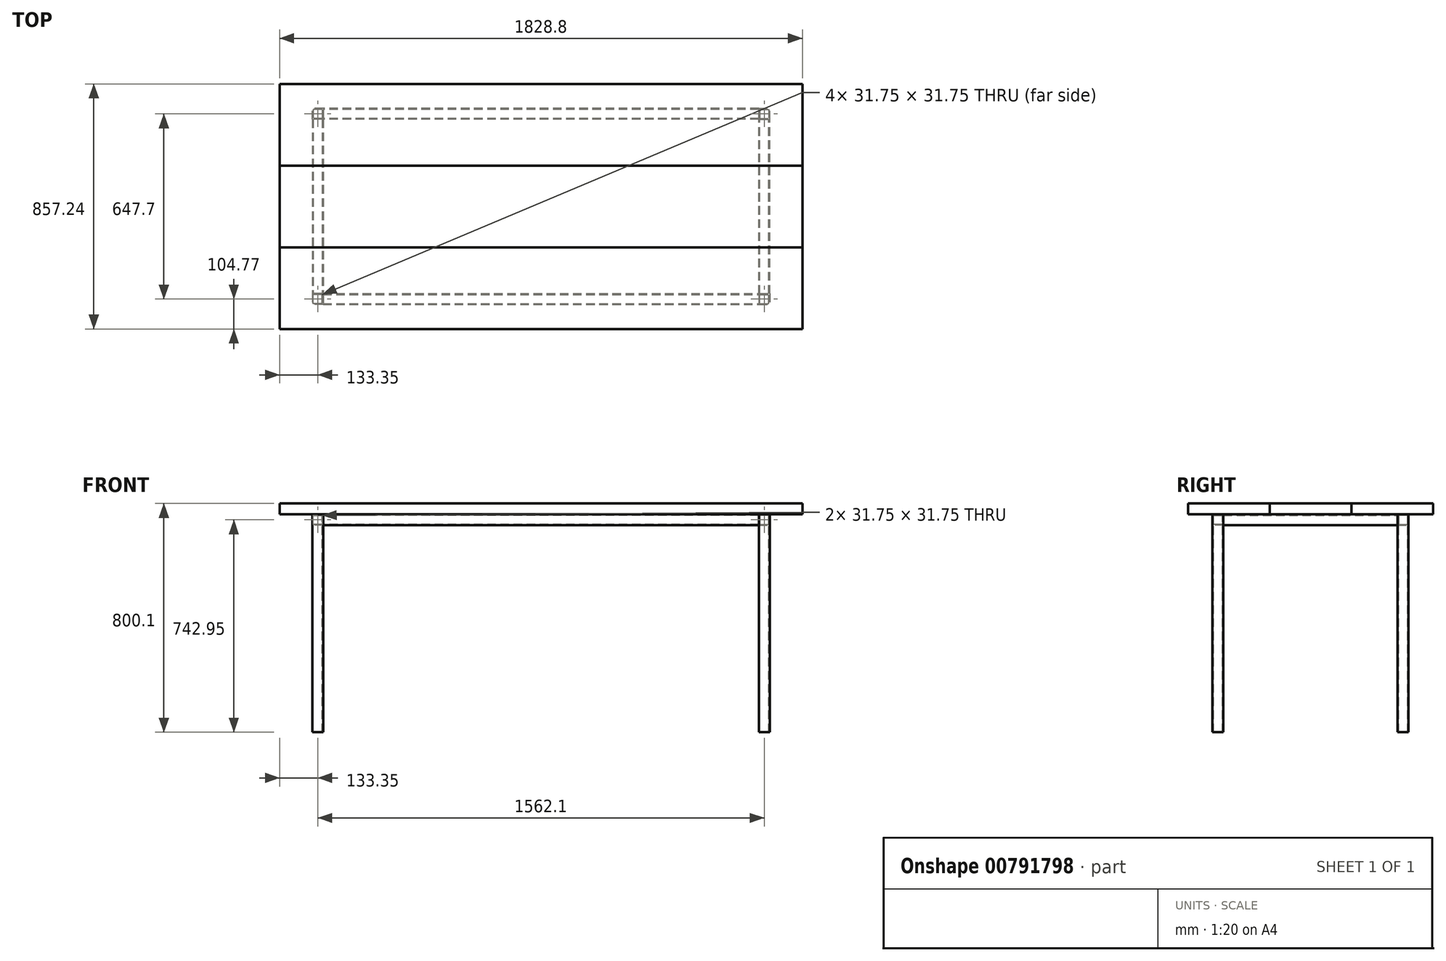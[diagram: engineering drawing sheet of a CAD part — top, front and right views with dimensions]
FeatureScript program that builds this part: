
annotation { "Feature Type Name" : "Feature", "Feature Type Description" : "" }
export const myFeature = defineFeature(function(context is Context, id is Id, definition is map)
    precondition{}
    {
        {
            var Q0;
            Q0=qCreatedBy(makeId("Top.planeOp"),FACE);
            var sketch = newSketch(context, id + "F0", { "sketchPlane" : qUnion([Q0])});
            skLineSegment(sketch, "E0.bottom", {"start": v(781.05, 323.85) * mm, "end": v(-781.05, 323.85) * mm});
            skLineSegment(sketch, "E0.top", {"start": v(781.05, -323.85) * mm, "end": v(-781.05, -323.85) * mm});
            skLineSegment(sketch, "E0.left", {"start": v(781.05, 323.85) * mm, "end": v(781.05, -323.85) * mm});
            skLineSegment(sketch, "E0.right", {"start": v(-781.05, 323.85) * mm, "end": v(-781.05, -323.85) * mm});
            skPoint(sketch, "E0.middle", {"position": v(0, 0) * mm});
            skSolve(sketch);
        }
        {
            var Q0;
            Q0=qCreatedBy(makeId("Front.planeOp"),FACE);
            var sketch = newSketch(context, id + "F1", { "sketchPlane" : qUnion([Q0])});
            skLineSegment(sketch, "E1.0", {"start": v(781.05, 0) * mm, "end": v(-781.05, 0) * mm});
            skLineSegment(sketch, "E2.bottom", {"start": v(-762, 19.05) * mm, "end": v(-800.1, 19.05) * mm});
            skLineSegment(sketch, "E2.top", {"start": v(-762, -19.05) * mm, "end": v(-800.1, -19.05) * mm});
            skLineSegment(sketch, "E2.left", {"start": v(-762, 19.05) * mm, "end": v(-762, -19.05) * mm});
            skLineSegment(sketch, "E2.right", {"start": v(-800.1, 19.05) * mm, "end": v(-800.1, -19.05) * mm});
            skPoint(sketch, "E2.middle", {"position": v(-781.05, 0) * mm});
            skLineSegment(sketch, "E3.bottom", {"start": v(-765.18, 15.87) * mm, "end": v(-796.93, 15.87) * mm});
            skLineSegment(sketch, "E3.top", {"start": v(-765.18, -15.88) * mm, "end": v(-796.93, -15.88) * mm});
            skLineSegment(sketch, "E3.left", {"start": v(-765.18, 15.87) * mm, "end": v(-765.18, -15.87) * mm});
            skLineSegment(sketch, "E3.right", {"start": v(-796.93, 15.87) * mm, "end": v(-796.93, -15.87) * mm});
            skSolve(sketch);
        }
        {
            var Q0;
            {var subQ1=sQuery(id+"F1.wireOp",EDGE,"E2.bottom");Q0=makeQuery(id+"F1.imprint","IMPRINT",FACE,{"disambiguationData":[TD([[makeQuery(id+"F1.imprint","IMPRINT",EDGE,{"derivedFrom":subQ1}),1.0]])]});}
            var Q1;
            Q1=sQuery(id+"F0.wireOp",EDGE,"E0.right");
            var Q2;
            Q2=sQuery(id+"F0.wireOp",EDGE,"E0.top");
            var Q3;
            Q3=sQuery(id+"F0.wireOp",EDGE,"E0.left");
            var Q4;
            Q4=sQuery(id+"F0.wireOp",EDGE,"E0.bottom");
            sweep(context, id + "F2", {"profiles" : qUnion([Q0]), "path" : qUnion([Q1, Q2, Q3, Q4])});
        }
        {
            var Q0;
            Q0=makeQuery(id+"F2.opSweep","SWEPT_FACE",FACE,{"disambiguationData":[OSD([sQuery(id+"F0.wireOp",EDGE,"E0.top"),sQuery(id+"F1.wireOp",EDGE,"E2.bottom")])]});
            var sketch = newSketch(context, id + "F3", { "sketchPlane" : qUnion([Q0])});
            skLineSegment(sketch, "E4.bottom", {"start": v(-762, 304.8) * mm, "end": v(-800.1, 304.8) * mm});
            skLineSegment(sketch, "E4.top", {"start": v(-762, 342.9) * mm, "end": v(-800.1, 342.9) * mm});
            skLineSegment(sketch, "E4.left", {"start": v(-762, 304.8) * mm, "end": v(-762, 342.9) * mm});
            skLineSegment(sketch, "E4.right", {"start": v(-800.1, 304.8) * mm, "end": v(-800.1, 342.9) * mm});
            skLineSegment(sketch, "E5.bottom", {"start": v(762, 304.8) * mm, "end": v(800.1, 304.8) * mm});
            skLineSegment(sketch, "E5.top", {"start": v(762, 342.9) * mm, "end": v(800.1, 342.9) * mm});
            skLineSegment(sketch, "E5.left", {"start": v(762, 304.8) * mm, "end": v(762, 342.9) * mm});
            skLineSegment(sketch, "E5.right", {"start": v(800.1, 304.8) * mm, "end": v(800.1, 342.9) * mm});
            skLineSegment(sketch, "E6.bottom", {"start": v(762, -304.8) * mm, "end": v(800.1, -304.8) * mm});
            skLineSegment(sketch, "E6.top", {"start": v(762, -342.9) * mm, "end": v(800.1, -342.9) * mm});
            skLineSegment(sketch, "E6.left", {"start": v(762, -304.8) * mm, "end": v(762, -342.9) * mm});
            skLineSegment(sketch, "E6.right", {"start": v(800.1, -304.8) * mm, "end": v(800.1, -342.9) * mm});
            skLineSegment(sketch, "E7.bottom", {"start": v(-762, -304.8) * mm, "end": v(-800.1, -304.8) * mm});
            skLineSegment(sketch, "E7.top", {"start": v(-762, -342.9) * mm, "end": v(-800.1, -342.9) * mm});
            skLineSegment(sketch, "E7.left", {"start": v(-762, -304.8) * mm, "end": v(-762, -342.9) * mm});
            skLineSegment(sketch, "E7.right", {"start": v(-800.1, -304.8) * mm, "end": v(-800.1, -342.9) * mm});
            skSolve(sketch);
        }
        {
            var Q0;
            Q0 = qSketchRegion(id + "F3", true);
            extrude(context, id + "F4", {"entities" : qUnion([Q0]), "operationType" : NewBodyOperationType.REMOVE, "oppositeDirection" : true, "depth" : 38.1 * mm, "offsetDistance" : 25.4 * mm});
        }
        {
            var Q0;
            Q0=makeQuery(id+"F4.boolean.opBoolean","SPLIT",FACE,{"disambiguationData":[TD([makeQuery(id+"F4.opExtrude","SWEPT_FACE",FACE,{"disambiguationData":[OSD([sQuery(id+"F3.wireOp",EDGE,"E4.left")])]})])],"derivedFrom":makeQuery(id+"F2.opSweep","SWEPT_FACE",FACE,{"disambiguationData":[OSD([sQuery(id+"F0.wireOp",EDGE,"E0.top"),sQuery(id+"F1.wireOp",EDGE,"E2.bottom")])]})});
            var sketch = newSketch(context, id + "F5", { "sketchPlane" : qUnion([Q0])});
            skLineSegment(sketch, "E8.bottom", {"start": v(-762, 304.8) * mm, "end": v(-800.1, 304.8) * mm});
            skLineSegment(sketch, "E8.top", {"start": v(-762, 342.9) * mm, "end": v(-800.1, 342.9) * mm});
            skLineSegment(sketch, "E8.left", {"start": v(-762, 304.8) * mm, "end": v(-762, 342.9) * mm});
            skLineSegment(sketch, "E8.right", {"start": v(-800.1, 304.8) * mm, "end": v(-800.1, 342.9) * mm});
            skLineSegment(sketch, "E9.bottom", {"start": v(-765.18, 339.73) * mm, "end": v(-796.93, 339.73) * mm});
            skLineSegment(sketch, "E9.top", {"start": v(-765.18, 307.98) * mm, "end": v(-796.93, 307.98) * mm});
            skLineSegment(sketch, "E9.left", {"start": v(-765.18, 339.73) * mm, "end": v(-765.18, 307.97) * mm});
            skLineSegment(sketch, "E9.right", {"start": v(-796.93, 339.73) * mm, "end": v(-796.93, 307.97) * mm});
            skPoint(sketch, "E9.middle", {"position": v(-781.05, 323.85) * mm});
            skPoint(sketch, "E9.middle.positionSnap0", {"position": v(-781.05, 342.9) * mm});
            skPoint(sketch, "E9.middle.positionSnap1", {"position": v(-762, 323.85) * mm});
            skPoint(sketch, "E9.centerSnap0", {"position": v(-781.05, 342.9) * mm});
            skPoint(sketch, "E9.centerSnap1", {"position": v(-762, 323.85) * mm});
            skLineSegment(sketch, "E10.MirrorCS", {"start": v(765.18, 339.73) * mm, "end": v(796.93, 339.73) * mm});
            skLineSegment(sketch, "E11.MirrorCS", {"start": v(762, 342.9) * mm, "end": v(800.1, 342.9) * mm});
            skLineSegment(sketch, "E12.MirrorCS", {"start": v(800.1, 304.8) * mm, "end": v(800.1, 342.9) * mm});
            skLineSegment(sketch, "E13.MirrorCS", {"start": v(796.93, 339.73) * mm, "end": v(796.93, 307.97) * mm});
            skLineSegment(sketch, "E14.MirrorCS", {"start": v(765.18, 307.98) * mm, "end": v(796.93, 307.98) * mm});
            skLineSegment(sketch, "E15.MirrorCS", {"start": v(762, 304.8) * mm, "end": v(800.1, 304.8) * mm});
            skLineSegment(sketch, "E16.MirrorCS", {"start": v(762, 304.8) * mm, "end": v(762, 342.9) * mm});
            skLineSegment(sketch, "E17.MirrorCS", {"start": v(765.18, 339.73) * mm, "end": v(765.18, 307.97) * mm});
            skLineSegment(sketch, "E18.MirrorCS", {"start": v(762, -342.9) * mm, "end": v(800.1, -342.9) * mm});
            skLineSegment(sketch, "E19.MirrorCS", {"start": v(765.18, -339.73) * mm, "end": v(796.93, -339.73) * mm});
            skLineSegment(sketch, "E20.MirrorCS", {"start": v(765.18, -307.98) * mm, "end": v(796.93, -307.98) * mm});
            skLineSegment(sketch, "E21.MirrorCS", {"start": v(765.18, -339.73) * mm, "end": v(765.18, -307.97) * mm});
            skLineSegment(sketch, "E22.MirrorCS", {"start": v(800.1, -304.8) * mm, "end": v(800.1, -342.9) * mm});
            skLineSegment(sketch, "E23.MirrorCS", {"start": v(762, -304.8) * mm, "end": v(762, -342.9) * mm});
            skLineSegment(sketch, "E24.MirrorCS", {"start": v(762, -304.8) * mm, "end": v(800.1, -304.8) * mm});
            skLineSegment(sketch, "E25.MirrorCS", {"start": v(796.93, -339.73) * mm, "end": v(796.93, -307.97) * mm});
            skLineSegment(sketch, "E26.MirrorCS", {"start": v(-765.18, -339.73) * mm, "end": v(-765.18, -307.97) * mm});
            skLineSegment(sketch, "E27.MirrorCS", {"start": v(-762, -342.9) * mm, "end": v(-800.1, -342.9) * mm});
            skLineSegment(sketch, "E28.MirrorCS", {"start": v(-762, -304.8) * mm, "end": v(-762, -342.9) * mm});
            skLineSegment(sketch, "E29.MirrorCS", {"start": v(-765.18, -339.73) * mm, "end": v(-796.93, -339.73) * mm});
            skPoint(sketch, "E30.MirrorP", {"position": v(-762, -323.85) * mm});
            skPoint(sketch, "E31.MirrorP", {"position": v(-781.05, -342.9) * mm});
            skLineSegment(sketch, "E32.MirrorCS", {"start": v(-796.93, -339.73) * mm, "end": v(-796.93, -307.97) * mm});
            skPoint(sketch, "E33.MirrorP", {"position": v(-781.05, -323.85) * mm});
            skLineSegment(sketch, "E34.MirrorCS", {"start": v(-765.18, -307.98) * mm, "end": v(-796.93, -307.98) * mm});
            skLineSegment(sketch, "E35.MirrorCS", {"start": v(-762, -304.8) * mm, "end": v(-800.1, -304.8) * mm});
            skLineSegment(sketch, "E36.MirrorCS", {"start": v(-800.1, -304.8) * mm, "end": v(-800.1, -342.9) * mm});
            skSolve(sketch);
        }
        {
            var Q0;
            Q0 = qSketchRegion(id + "F5", true);
            extrude(context, id + "F6", {"entities" : qUnion([Q0]), "oppositeDirection" : true, "depth" : 762 * mm, "offsetDistance" : 25.4 * mm});
        }
        {
            var Q0;
            Q0=qCreatedBy(makeId("Right.planeOp"),FACE);
            var sketch = newSketch(context, id + "F7", { "sketchPlane" : qUnion([Q0])});
            skLineSegment(sketch, "E37.0", {"start": v(-304.8, 19.05) * mm, "end": v(304.8, 19.05) * mm});
            skLineSegment(sketch, "E38.bottom", {"start": v(-142.88, 19.05) * mm, "end": v(142.87, 19.05) * mm});
            skLineSegment(sketch, "E38.top", {"start": v(-142.88, 57.15) * mm, "end": v(142.87, 57.15) * mm});
            skLineSegment(sketch, "E38.left", {"start": v(-142.88, 19.05) * mm, "end": v(-142.88, 57.15) * mm});
            skLineSegment(sketch, "E38.right", {"start": v(142.87, 19.05) * mm, "end": v(142.87, 57.15) * mm});
            skSolve(sketch);
        }
        {
            var Q0;
            Q0 = qSketchRegion(id + "F7", true);
            extrude(context, id + "F8", {"entities" : qUnion([Q0]), "depth" : 914.4 * mm, "offsetDistance" : 25.4 * mm, "hasSecondDirection" : true, "secondDirectionOppositeDirection" : true, "secondDirectionDepth" : 914.4 * mm});
        }
        {
            var Q0;
            Q0=qCreatedBy(makeId("Right.planeOp"),FACE);
            var sketch = newSketch(context, id + "F9", { "sketchPlane" : qUnion([Q0])});
            skLineSegment(sketch, "E39.0", {"start": v(142.87, 19.05) * mm, "end": v(142.87, 57.15) * mm});
            skLineSegment(sketch, "E40.bottom", {"start": v(142.87, 57.15) * mm, "end": v(428.62, 57.15) * mm});
            skLineSegment(sketch, "E40.top", {"start": v(142.87, 19.05) * mm, "end": v(428.62, 19.05) * mm});
            skLineSegment(sketch, "E40.left", {"start": v(142.87, 57.15) * mm, "end": v(142.87, 19.05) * mm});
            skLineSegment(sketch, "E40.right", {"start": v(428.62, 57.15) * mm, "end": v(428.62, 19.05) * mm});
            skLineSegment(sketch, "E41.MirrorCS", {"start": v(-142.87, 57.15) * mm, "end": v(-142.87, 19.05) * mm});
            skLineSegment(sketch, "E42.MirrorCS", {"start": v(-428.62, 57.15) * mm, "end": v(-428.62, 19.05) * mm});
            skLineSegment(sketch, "E43.MirrorCS", {"start": v(-142.87, 19.05) * mm, "end": v(-428.62, 19.05) * mm});
            skLineSegment(sketch, "E44.MirrorCS", {"start": v(-142.87, 57.15) * mm, "end": v(-428.62, 57.15) * mm});
            skLineSegment(sketch, "E45.MirrorCS", {"start": v(-142.87, 19.05) * mm, "end": v(-142.87, 57.15) * mm});
            skSolve(sketch);
        }
        {
            var Q0;
            Q0 = qSketchRegion(id + "F9", true);
            extrude(context, id + "F10", {"entities" : qUnion([Q0]), "depth" : 914.4 * mm, "offsetDistance" : 25.4 * mm, "hasSecondDirection" : true, "secondDirectionOppositeDirection" : true, "secondDirectionDepth" : 914.4 * mm});
        }
    });
